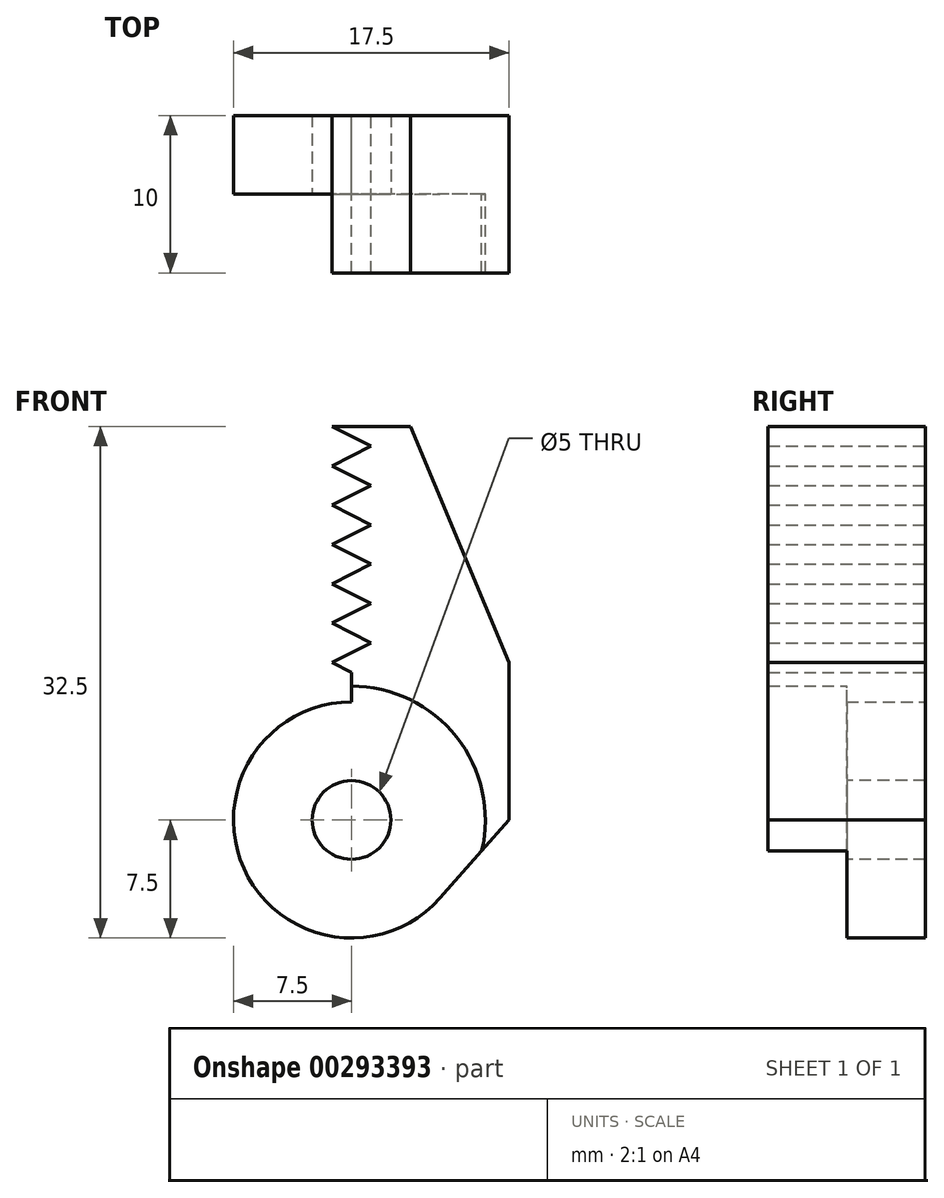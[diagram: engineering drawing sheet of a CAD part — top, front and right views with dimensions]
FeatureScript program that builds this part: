
annotation { "Feature Type Name" : "Feature", "Feature Type Description" : "" }
export const myFeature = defineFeature(function(context is Context, id is Id, definition is map)
    precondition{}
    {
        {
            var Q0;
            Q0=qCreatedBy(makeId("Front.planeOp"),FACE);
            var sketch = newSketch(context, id + "F0", { "sketchPlane" : qUnion([Q0])});
            skArc(sketch, "E0", {"start": v(0, 7.5) * mm, "mid": v(-6.84, -3.09) * mm, "end": v(5.63, -4.96) * mm});
            skLineSegment(sketch, "E1", {"start": v(0, 7.5) * mm, "end": v(0, 9.13) * mm});
            skLineSegment(sketch, "E2", {"start": v(0, 9.13) * mm, "end": v(1.25, 10) * mm});
            skLineSegment(sketch, "E3", {"start": v(1.25, 10) * mm, "end": v(1.25, 25) * mm});
            skLineSegment(sketch, "E4", {"start": v(1.25, 25) * mm, "end": v(3.75, 25) * mm});
            skLineSegment(sketch, "E5", {"start": v(3.75, 25) * mm, "end": v(10, 10) * mm});
            skLineSegment(sketch, "E6", {"start": v(10, 10) * mm, "end": v(10, 0) * mm});
            skLineSegment(sketch, "E7", {"start": v(10, 0) * mm, "end": v(5.62, -4.96) * mm});
            skLineSegment(sketch, "E8", {"start": v(1.25, 25) * mm, "end": v(1.25, 10) * mm});
            skLineSegment(sketch, "E9", {"start": v(1.25, 10) * mm, "end": v(10, 10) * mm, "construction": true});
            skLineSegment(sketch, "E10", {"start": v(0, 0) * mm, "end": v(10, 0) * mm, "construction": true});
            skLineSegment(sketch, "E11", {"start": v(0, 9.13) * mm, "end": v(0, 25) * mm, "construction": true});
            skSolve(sketch);
        }
        {
            var Q0;
            Q0=makeQuery(id+"F0.imprint","IMPRINT",FACE,{"disambiguationData":[TD([[makeQuery(id+"F0.imprint","IMPRINT",EDGE,{"derivedFrom":sQuery(id+"F0.wireOp",EDGE,"E0")}),1.0]])]});
            extrude(context, id + "F1", {"entities" : qUnion([Q0]), "depth" : 5 * mm});
        }
        {
            var Q0;
            Q0=makeQuery(id+"F1.opExtrude","CAP_FACE",FACE,{"disambiguationData":[OSD([sQuery(id+"F0.wireOp",EDGE,"E0"),sQuery(id+"F0.wireOp",EDGE,"E1"),sQuery(id+"F0.wireOp",EDGE,"E2"),sQuery(id+"F0.wireOp",EDGE,"E4"),sQuery(id+"F0.wireOp",EDGE,"E5"),sQuery(id+"F0.wireOp",EDGE,"E6"),sQuery(id+"F0.wireOp",EDGE,"E7"),sQuery(id+"F0.wireOp",EDGE,"E8")])],"isStart":false});
            var sketch = newSketch(context, id + "F2", { "sketchPlane" : qUnion([Q0])});
            skLineSegment(sketch, "E12", {"start": v(1.25, 25) * mm, "end": v(1.25, 22.5) * mm});
            skLineSegment(sketch, "E13", {"start": v(1.25, 23.75) * mm, "end": v(-1.25, 25) * mm});
            skPoint(sketch, "E13.endSnap0", {"position": v(1.25, 23.75) * mm});
            skLineSegment(sketch, "E14", {"start": v(1.25, 9.13) * mm, "end": v(1.25, 24.37) * mm, "construction": true});
            skLineSegment(sketch, "E15.0.1.0", {"start": v(-1.25, 22.5) * mm, "end": v(1.25, 23.75) * mm});
            skLineSegment(sketch, "E15.0.1.1", {"start": v(1.25, 21.25) * mm, "end": v(-1.25, 22.5) * mm});
            skLineSegment(sketch, "E15.0.1.2", {"start": v(0, 6.63) * mm, "end": v(0, 7.5) * mm, "construction": true});
            skLineSegment(sketch, "E15.0.2.0", {"start": v(-1.25, 20) * mm, "end": v(1.25, 21.25) * mm});
            skLineSegment(sketch, "E15.0.2.1", {"start": v(1.25, 18.75) * mm, "end": v(-1.25, 20) * mm});
            skLineSegment(sketch, "E15.0.2.2", {"start": v(0, 4.13) * mm, "end": v(0, 8.5) * mm, "construction": true});
            skLineSegment(sketch, "E15.0.3.0", {"start": v(-1.25, 17.5) * mm, "end": v(1.25, 18.75) * mm});
            skLineSegment(sketch, "E15.0.3.1", {"start": v(1.25, 16.25) * mm, "end": v(-1.25, 17.5) * mm});
            skLineSegment(sketch, "E15.0.3.2", {"start": v(0, 1.63) * mm, "end": v(0, 8.5) * mm, "construction": true});
            skLineSegment(sketch, "E15.0.4.0", {"start": v(-1.25, 15) * mm, "end": v(1.25, 16.25) * mm});
            skLineSegment(sketch, "E15.0.4.1", {"start": v(1.25, 13.75) * mm, "end": v(-1.25, 15) * mm});
            skLineSegment(sketch, "E15.0.4.2", {"start": v(0, -0.87) * mm, "end": v(0, 7.5) * mm, "construction": true});
            skLineSegment(sketch, "E15.0.5.0", {"start": v(-1.25, 12.5) * mm, "end": v(1.25, 13.75) * mm});
            skLineSegment(sketch, "E15.0.5.1", {"start": v(1.25, 11.25) * mm, "end": v(-1.25, 12.5) * mm});
            skLineSegment(sketch, "E15.0.5.2", {"start": v(0, -3.37) * mm, "end": v(0, 9.13) * mm, "construction": true});
            skLineSegment(sketch, "E15.direction1", {"start": v(0, 9.13) * mm, "end": v(25, 9.13) * mm, "construction": true});
            skLineSegment(sketch, "E15.direction2", {"start": v(0, 8.5) * mm, "end": v(0, 6.63) * mm, "construction": true});
            skCircle(sketch, "E16", {"center": v(0, 0) * mm, "radius": 7.5 * mm, "construction": true});
            skArc(sketch, "E17.0", {"start": v(8.27, -1.96) * mm, "mid": v(6.67, 5.27) * mm, "end": v(0, 8.5) * mm});
            skLineSegment(sketch, "E18", {"start": v(10, 0) * mm, "end": v(5.63, -4.96) * mm});
            skLineSegment(sketch, "E19.trimOffspring", {"start": v(0, 11.05) * mm, "end": v(0, 24.37) * mm, "construction": true});
            skLineSegment(sketch, "E20.trimOffspring", {"start": v(0, 8.55) * mm, "end": v(0, 9.13) * mm, "construction": true});
            skLineSegment(sketch, "E21", {"start": v(0, 9.13) * mm, "end": v(0, 8.5) * mm});
            skLineSegment(sketch, "E22", {"start": v(10, 0) * mm, "end": v(10, 10) * mm});
            skLineSegment(sketch, "E23", {"start": v(10, 10) * mm, "end": v(3.75, 25) * mm});
            skLineSegment(sketch, "E24", {"start": v(3.75, 25) * mm, "end": v(1.25, 25) * mm});
            skLineSegment(sketch, "E25", {"start": v(1.25, 25) * mm, "end": v(-1.25, 25) * mm});
            skLineSegment(sketch, "E26", {"start": v(1.25, 11.25) * mm, "end": v(1.25, 9.13) * mm, "construction": true});
            skLineSegment(sketch, "E27", {"start": v(1.25, 9.13) * mm, "end": v(1.25, 11.25) * mm, "construction": true});
            skLineSegment(sketch, "E28.0.1.0", {"start": v(-1.25, 10) * mm, "end": v(1.25, 11.25) * mm});
            skLineSegment(sketch, "E28.0.1.1", {"start": v(0, 9.37) * mm, "end": v(-1.25, 10) * mm});
            skLineSegment(sketch, "E28.1.0.0", {"start": v(16.35, 12.5) * mm, "end": v(18.85, 13.75) * mm});
            skLineSegment(sketch, "E28.1.0.1", {"start": v(18.85, 11.25) * mm, "end": v(16.35, 12.5) * mm});
            skLineSegment(sketch, "E28.1.1.0", {"start": v(16.35, 10) * mm, "end": v(18.85, 11.25) * mm});
            skLineSegment(sketch, "E28.1.1.1", {"start": v(18.85, 8.75) * mm, "end": v(16.35, 10) * mm});
            skLineSegment(sketch, "E28.2.0.0", {"start": v(33.95, 12.5) * mm, "end": v(36.45, 13.75) * mm});
            skLineSegment(sketch, "E28.2.0.1", {"start": v(36.45, 11.25) * mm, "end": v(33.95, 12.5) * mm});
            skLineSegment(sketch, "E28.2.1.0", {"start": v(33.95, 10) * mm, "end": v(36.45, 11.25) * mm});
            skLineSegment(sketch, "E28.2.1.1", {"start": v(36.45, 8.75) * mm, "end": v(33.95, 10) * mm});
            skLineSegment(sketch, "E28.direction1", {"start": v(-1.25, 12.5) * mm, "end": v(16.35, 12.5) * mm, "construction": true});
            skLineSegment(sketch, "E28.direction2", {"start": v(-1.25, 12.5) * mm, "end": v(-1.25, 10) * mm, "construction": true});
            skPoint(sketch, "E29.orphan", {"position": v(1.25, 8.75) * mm});
            skLineSegment(sketch, "E30.trimOffspring", {"start": v(0, 9.37) * mm, "end": v(0, 16.87) * mm, "construction": true});
            skLineSegment(sketch, "E31.trimOffspring", {"start": v(0, 9.37) * mm, "end": v(0, 19.37) * mm, "construction": true});
            skLineSegment(sketch, "E32.trimOffspring", {"start": v(0, 9.37) * mm, "end": v(0, 11.87) * mm, "construction": true});
            skLineSegment(sketch, "E33.trimOffspring", {"start": v(0, 9.37) * mm, "end": v(0, 14.37) * mm, "construction": true});
            skLineSegment(sketch, "E34", {"start": v(0, 9.37) * mm, "end": v(0, 9.13) * mm});
            skSolve(sketch);
        }
        {
            var Q0;
            Q0 = qSketchRegion(id + "F2", true);
            extrude(context, id + "F3", {"entities" : qUnion([Q0]), "operationType" : NewBodyOperationType.ADD, "depth" : 5 * mm, "hasSecondDirection" : true, "secondDirectionOppositeDirection" : true, "secondDirectionDepth" : 5 * mm});
        }
        {
            var Q0;
            Q0=makeQuery(id+"F1.opExtrude","CAP_FACE",FACE,{"disambiguationData":[OSD([sQuery(id+"F0.wireOp",EDGE,"E0"),sQuery(id+"F0.wireOp",EDGE,"E1"),sQuery(id+"F0.wireOp",EDGE,"E2"),sQuery(id+"F0.wireOp",EDGE,"E4"),sQuery(id+"F0.wireOp",EDGE,"E5"),sQuery(id+"F0.wireOp",EDGE,"E6"),sQuery(id+"F0.wireOp",EDGE,"E7"),sQuery(id+"F0.wireOp",EDGE,"E8")])],"isStart":false});
            var sketch = newSketch(context, id + "F4", { "sketchPlane" : qUnion([Q0])});
            skCircle(sketch, "E35", {"center": v(0, 0) * mm, "radius": 2.5 * mm});
            skSolve(sketch);
        }
        {
            var Q0;
            Q0=makeQuery(id+"F4.imprint","IMPRINT",FACE,{"disambiguationData":[TD([[makeQuery(id+"F4.imprint","IMPRINT",EDGE,{"derivedFrom":sQuery(id+"F4.wireOp",EDGE,"E35")}),1.0]])]});
            extrude(context, id + "F5", {"entities" : qUnion([Q0]), "operationType" : NewBodyOperationType.REMOVE, "endBound" : BoundingType.THROUGH_ALL, "oppositeDirection" : true, "depth" : 25 * mm});
        }
        {
            var Q0;
            Q0=makeQuery(id+"F1.opExtrude","SWEPT_BODY",BODY,{"disambiguationData":[OSD([sQuery(id+"F0.wireOp",EDGE,"E0"),sQuery(id+"F0.wireOp",EDGE,"E1"),sQuery(id+"F0.wireOp",EDGE,"E2"),sQuery(id+"F0.wireOp",EDGE,"E4"),sQuery(id+"F0.wireOp",EDGE,"E5"),sQuery(id+"F0.wireOp",EDGE,"E6"),sQuery(id+"F0.wireOp",EDGE,"E7"),sQuery(id+"F0.wireOp",EDGE,"E8")])]});
            transform(context, id + "F6", {"entities" : qUnion([Q0]), "transformType" : TransformType.TRANSLATION_3D, "dx" : 0 * mm, "dy" : 0 * mm, "dz" : 0 * mm, "makeCopy" : true});
        }
        {
            var Q0;
            Q0=makeQuery(id+"F6.opPattern","COPY",BODY,{"derivedFrom":makeQuery(id+"F1.opExtrude","SWEPT_BODY",BODY,{"disambiguationData":[OSD([sQuery(id+"F0.wireOp",EDGE,"E0"),sQuery(id+"F0.wireOp",EDGE,"E1"),sQuery(id+"F0.wireOp",EDGE,"E2"),sQuery(id+"F0.wireOp",EDGE,"E4"),sQuery(id+"F0.wireOp",EDGE,"E5"),sQuery(id+"F0.wireOp",EDGE,"E6"),sQuery(id+"F0.wireOp",EDGE,"E7"),sQuery(id+"F0.wireOp",EDGE,"E8")])]}),"instanceName":"1"});
            deleteBodies(context, id + "F7", {"entities" : qUnion([Q0])});
        }
        {
            var Q0;
            Q0=makeQuery(id+"F1.opExtrude","SWEPT_BODY",BODY,{"disambiguationData":[OSD([sQuery(id+"F0.wireOp",EDGE,"E0"),sQuery(id+"F0.wireOp",EDGE,"E1"),sQuery(id+"F0.wireOp",EDGE,"E2"),sQuery(id+"F0.wireOp",EDGE,"E4"),sQuery(id+"F0.wireOp",EDGE,"E5"),sQuery(id+"F0.wireOp",EDGE,"E6"),sQuery(id+"F0.wireOp",EDGE,"E7"),sQuery(id+"F0.wireOp",EDGE,"E8")])]});
            transform(context, id + "F8", {"entities" : qUnion([Q0]), "transformType" : TransformType.TRANSLATION_3D, "dx" : 20 * mm, "dy" : 0 * mm, "dz" : 0 * mm, "makeCopy" : true});
        }
        {
            var Q0;
            Q0=makeQuery(id+"F8.opPattern","COPY",BODY,{"derivedFrom":makeQuery(id+"F1.opExtrude","SWEPT_BODY",BODY,{"disambiguationData":[OSD([sQuery(id+"F0.wireOp",EDGE,"E0"),sQuery(id+"F0.wireOp",EDGE,"E1"),sQuery(id+"F0.wireOp",EDGE,"E2"),sQuery(id+"F0.wireOp",EDGE,"E4"),sQuery(id+"F0.wireOp",EDGE,"E5"),sQuery(id+"F0.wireOp",EDGE,"E6"),sQuery(id+"F0.wireOp",EDGE,"E7"),sQuery(id+"F0.wireOp",EDGE,"E8")])]}),"instanceName":"1"});
            deleteBodies(context, id + "F9", {"entities" : qUnion([Q0])});
        }
        {
            var Q0;
            Q0=makeQuery(id+"F1.opExtrude","SWEPT_BODY",BODY,{"disambiguationData":[OSD([sQuery(id+"F0.wireOp",EDGE,"E0"),sQuery(id+"F0.wireOp",EDGE,"E1"),sQuery(id+"F0.wireOp",EDGE,"E2"),sQuery(id+"F0.wireOp",EDGE,"E4"),sQuery(id+"F0.wireOp",EDGE,"E5"),sQuery(id+"F0.wireOp",EDGE,"E6"),sQuery(id+"F0.wireOp",EDGE,"E7"),sQuery(id+"F0.wireOp",EDGE,"E8")])]});
            transform(context, id + "F10", {"entities" : qUnion([Q0]), "transformType" : TransformType.TRANSLATION_3D, "dx" : 0 * mm, "dy" : 0 * mm, "dz" : 0 * mm, "makeCopy" : true});
        }
        {
            var Q0;
            Q0=makeQuery(id+"F10.opPattern","COPY",BODY,{"derivedFrom":makeQuery(id+"F1.opExtrude","SWEPT_BODY",BODY,{"disambiguationData":[OSD([sQuery(id+"F0.wireOp",EDGE,"E0"),sQuery(id+"F0.wireOp",EDGE,"E1"),sQuery(id+"F0.wireOp",EDGE,"E2"),sQuery(id+"F0.wireOp",EDGE,"E4"),sQuery(id+"F0.wireOp",EDGE,"E5"),sQuery(id+"F0.wireOp",EDGE,"E6"),sQuery(id+"F0.wireOp",EDGE,"E7"),sQuery(id+"F0.wireOp",EDGE,"E8")])]}),"instanceName":"1"});
            deleteBodies(context, id + "F11", {"entities" : qUnion([Q0])});
        }
    });
